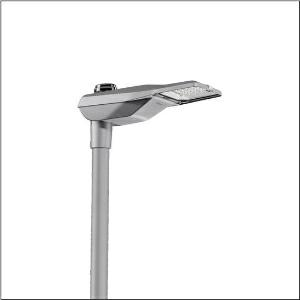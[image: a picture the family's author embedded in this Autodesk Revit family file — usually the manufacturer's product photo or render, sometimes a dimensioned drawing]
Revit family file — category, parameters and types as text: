
# Revit family: streetlight_sl_21_micro___st0_8a_5xe5c37n08cb_a39a
name_source: partatom
category: Lighting Fixtures
units: mm (PartAtom-declared; Revit-internal decimal feet)

## family parameters
Cut with Voids When Loaded = No
Host = Face
Light Source = No
Part Type = Normal
Room Calculation Point = No
Round Connector Dimension = Use Diameter
Shared = No

## types (1)
- --- (1 x LED, 2290 lm, 15.8 W, 3000K)
    Apparent Load = 16 VA
    CIE Flux Codes = 38 75 97 100 100
    Color Rendering = 70
    Color Temperature = 3000K
    Default Elevation = 1800 mm
    Description = Streetlight SL 21 micro, mast luminaire, primary light control with lens, of PMMA, primary optical cover: cover, of toughened safety glass, transparent, light distribution: ST0.8a, light emission: direct distribution, primary light characteristic: asymmetric, installation type: post-top, LED, 3G 1.5mm², High Power LED, rated luminous flux: 2.290lm, luminous efficacy: 145lm/W, light colour: 730, colour temperature: 3000K, control: overheat protection, presetting dimming linear, constant luminous flux control, time-dependent luminous flux control, flexible luminous flux parameterisation, mains connection: 230..240V, AC, 50/60Hz, connection cable pre-assembled, cable length: 6,5m, wiring characteristics: H07RN-F, start of lifetime: 16W, end of service life: 16W, reduction: 8W, luminaire housing, of diecast aluminium (EN AC-44300), powder-coated, Siteco® metallic grey (DB 702S), corrosivity category C5 mid according to DIN EN ISO 12944, multi-level sealing system, sealing non-destructively replaceable, inclination adjustable: 0°, 5°, 10°, 15°, length: 528mm, width: 235mm, height: 110mm, spigot size: 76/60mm (post-top), protection rating (complete): IP66, insulation class (complete): insulation class I (protective earthing), certification: CE, ENEC, ENEC+, VDE, impact resistance: IK09, permissible operating ambient temperature for outdoor applications: -40..+50°C, standard-compliant lighting for roads and squares, packaging unit: 1 piece

Light Distribution: ST0.8a
    Height = 110 mm
    Lamp = 1 x LED
    Lamp Light Flux = 2290 lm
    Lamp Power = 15.8 W
    Lamp count = 1
    Length = 528 mm
    Luminous efficacy = 145 lm/W
    Manufacturer = Siteco
    ModVariant = No
    Model = 5XE5C37N08CB
    Number of Poles = 1
    OnlyDefault = Yes
    Power Factor = 1
    Product Name = Streetlight SL 21 micro | ST0.8a
    Product group = mast luminaire | pylon top
    ProductGroupID = 6100
    Protection Class = Protection class I
    Protection Degree = IP 66
    RLX_Detail_Level = 1
    RLX_Emergency_Light_Flux = 0 lm
    RLX_Emergency_Type = 0
    RLX_Emergency_Type_DB = No
    RlxData = <blob elided: 98265 chars, md5=1e38148c>
    Socket = socket
    Standby Power = 0 W
    System Light Flux = 2290 lm
    System Power = 16 W
    Type Comments = factory setting: luminous flux: 100 % | dim-lin: 254 | 300 mA
    Type Image = l_1294375.jpg
    URL = http://relux.com
    VarID = @adj_083789
    Voltage = 0 V
    Weight = 0.00 kg
    Width = 235 mm

## geometry (parser evidence)
native form markers: Blend x4, Sweep x11
no freeform markers — native parametric forms only
